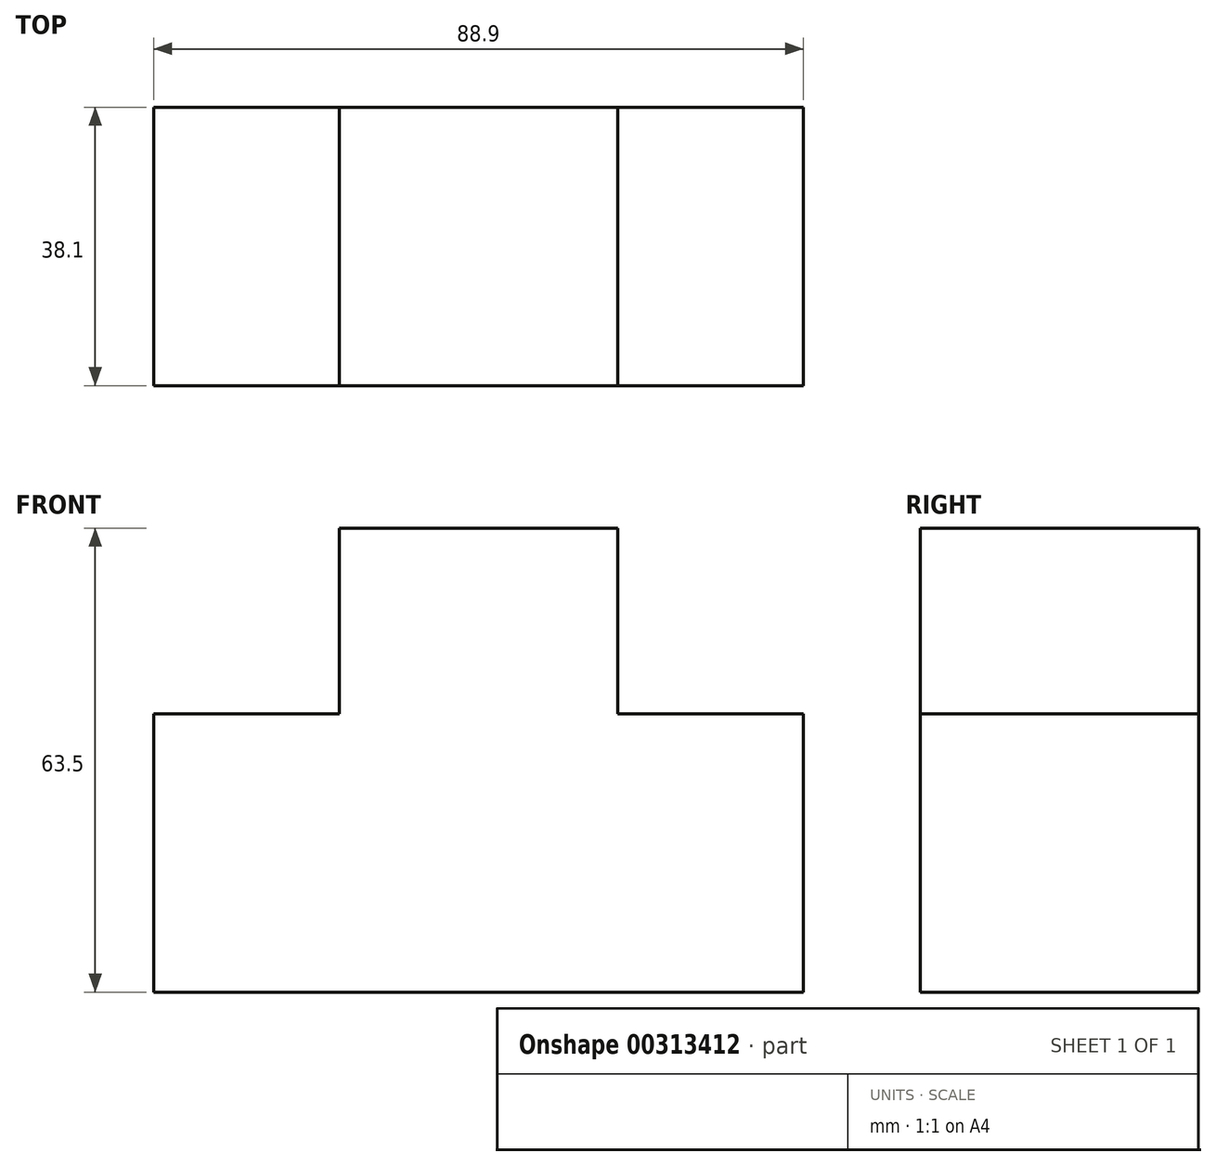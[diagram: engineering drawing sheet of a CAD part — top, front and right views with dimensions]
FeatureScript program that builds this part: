
annotation { "Feature Type Name" : "Feature", "Feature Type Description" : "" }
export const myFeature = defineFeature(function(context is Context, id is Id, definition is map)
    precondition{}
    {
        {
            var Q0;
            Q0=qCreatedBy(makeId("Front.planeOp"),FACE);
            var sketch = newSketch(context, id + "F0", { "sketchPlane" : qUnion([Q0])});
            skLineSegment(sketch, "E0", {"start": v(-25.4, -37.78) * mm, "end": v(63.5, -37.78) * mm});
            skLineSegment(sketch, "E1", {"start": v(63.5, -37.78) * mm, "end": v(63.5, 0.32) * mm});
            skLineSegment(sketch, "E2", {"start": v(63.5, 0.32) * mm, "end": v(38.1, 0.32) * mm});
            skLineSegment(sketch, "E3", {"start": v(38.1, 0.32) * mm, "end": v(38.1, 25.72) * mm});
            skLineSegment(sketch, "E4", {"start": v(38.1, 25.72) * mm, "end": v(0, 25.72) * mm});
            skLineSegment(sketch, "E5", {"start": v(0, 25.72) * mm, "end": v(0, 0.32) * mm});
            skLineSegment(sketch, "E6", {"start": v(0, 0.32) * mm, "end": v(-25.4, 0.32) * mm});
            skLineSegment(sketch, "E7", {"start": v(-25.4, 0.32) * mm, "end": v(-25.4, -37.78) * mm});
            skSolve(sketch);
        }
        {
            var Q0;
            Q0=makeQuery(id+"F0.imprint","IMPRINT",FACE,{"disambiguationData":[TD([[makeQuery(id+"F0.imprint","IMPRINT",EDGE,{"derivedFrom":sQuery(id+"F0.wireOp",EDGE,"E0")}),1.0]])]});
            extrude(context, id + "F1", {"entities" : qUnion([Q0]), "depth" : 38.1 * mm});
        }
    });
